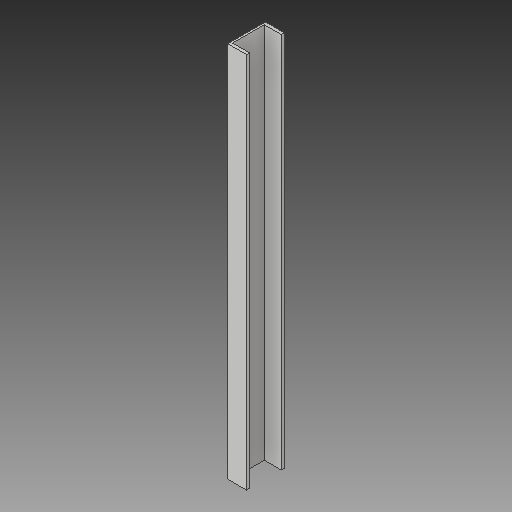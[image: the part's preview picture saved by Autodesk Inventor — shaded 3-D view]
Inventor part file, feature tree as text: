
AUTODESK INVENTOR PART (.ipt)
format: ipt  version: 2019 (Build 230136000, 136)  size: 96,768 bytes
history: native  units: mm
features: extrude x1, mirror x1, sketch x1
ambient origin geometry x8: Origin, YZ Plane, XZ Plane, XY Plane, X Axis, Y Axis, Z Axis, Center Point
bodies: Solid1 (feature_tree)
feature tree (3):
  extrude  "Extrusion1"  Depth=100.0mm
  mirror  "Mirror1"
  sketch  "Sketch1"  dims[d0=50.0mm d1=100.0mm d2=8.0mm d3=45.0mm d4=84.0mm d5=500.0mm d6=0.0mm]
